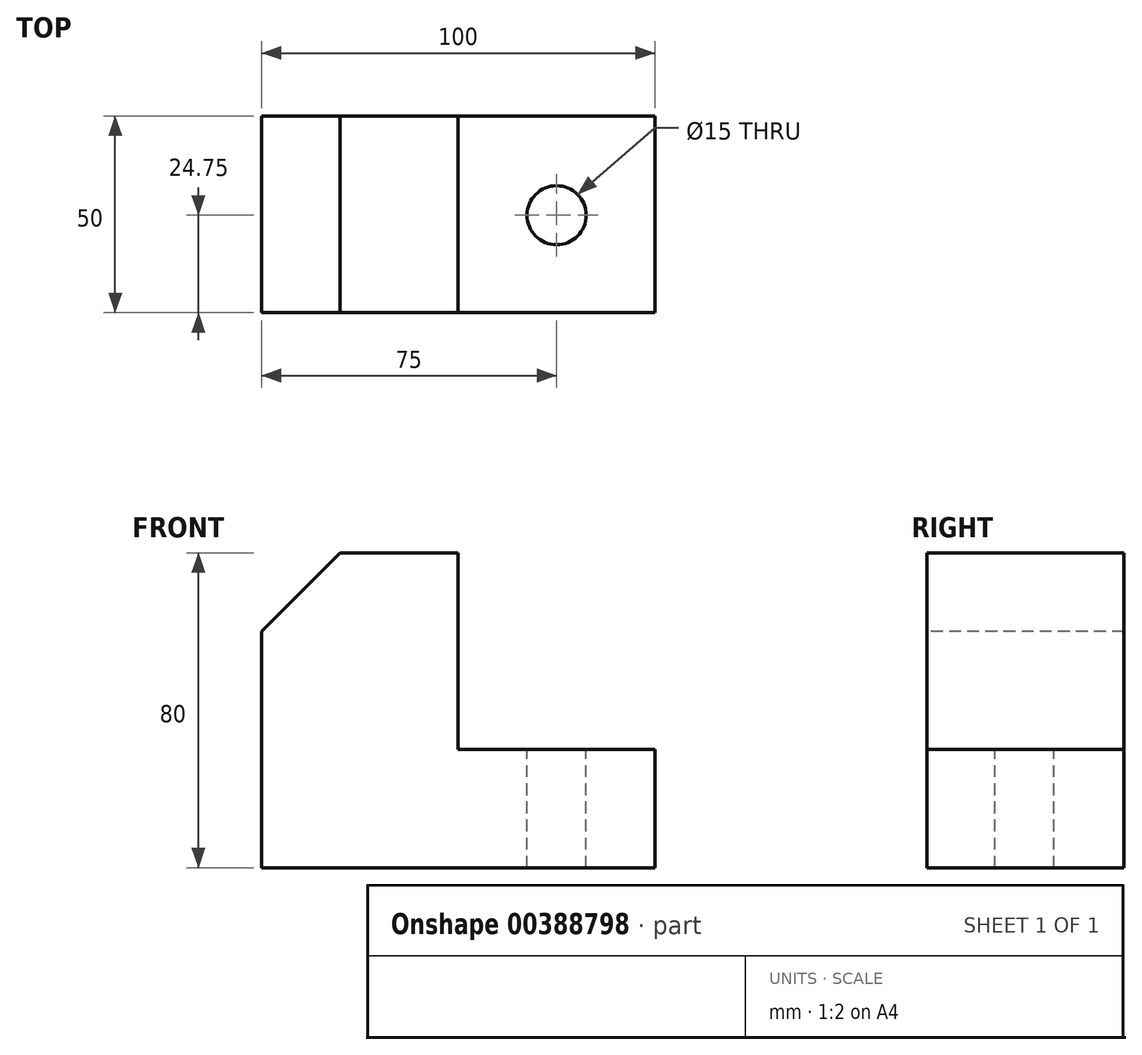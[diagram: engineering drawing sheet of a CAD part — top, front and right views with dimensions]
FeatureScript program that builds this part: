
annotation { "Feature Type Name" : "Feature", "Feature Type Description" : "" }
export const myFeature = defineFeature(function(context is Context, id is Id, definition is map)
    precondition{}
    {
        {
            var Q0;
            Q0=qCreatedBy(makeId("Top.planeOp"),FACE);
            var sketch = newSketch(context, id + "F0", { "sketchPlane" : qUnion([Q0])});
            skLineSegment(sketch, "E0.bottom", {"start": v(0, 0) * mm, "end": v(100, 0) * mm});
            skLineSegment(sketch, "E0.top", {"start": v(0, 50) * mm, "end": v(100, 50) * mm});
            skLineSegment(sketch, "E0.left", {"start": v(0, 0) * mm, "end": v(0, 50) * mm});
            skLineSegment(sketch, "E0.right", {"start": v(100, 0) * mm, "end": v(100, 50) * mm});
            skSolve(sketch);
        }
        {
            var Q0;
            Q0=makeQuery(id+"F0.imprint","IMPRINT",FACE,{"disambiguationData":[TD([[makeQuery(id+"F0.imprint","IMPRINT",EDGE,{"derivedFrom":sQuery(id+"F0.wireOp",EDGE,"E0.bottom")}),1.0]])]});
            extrude(context, id + "F1", {"entities" : qUnion([Q0]), "depth" : 30 * mm});
        }
        {
            var Q0;
            Q0=makeQuery(id+"F1.opExtrude","CAP_FACE",FACE,{"disambiguationData":[OSD([sQuery(id+"F0.wireOp",EDGE,"E0.bottom"),sQuery(id+"F0.wireOp",EDGE,"E0.top"),sQuery(id+"F0.wireOp",EDGE,"E0.left"),sQuery(id+"F0.wireOp",EDGE,"E0.right")])],"isStart":false});
            var sketch = newSketch(context, id + "F2", { "sketchPlane" : qUnion([Q0])});
            skLineSegment(sketch, "E1.bottom", {"start": v(0, 0) * mm, "end": v(50, 0) * mm});
            skLineSegment(sketch, "E1.top", {"start": v(0, 50) * mm, "end": v(50, 50) * mm});
            skLineSegment(sketch, "E1.left", {"start": v(0, 0) * mm, "end": v(0, 50) * mm});
            skLineSegment(sketch, "E1.right", {"start": v(50, 0) * mm, "end": v(50, 50) * mm});
            skSolve(sketch);
        }
        {
            var Q0;
            Q0 = qSketchRegion(id + "F2", true);
            extrude(context, id + "F3", {"entities" : qUnion([Q0]), "operationType" : NewBodyOperationType.ADD, "depth" : 50 * mm});
        }
        {
            var Q0;
            Q0=makeQuery(id+"F3.boolean.opBoolean","MERGE",FACE,{"derivedFrom":[makeQuery(id+"F1.opExtrude","SWEPT_FACE",FACE,{"disambiguationData":[OSD([sQuery(id+"F0.wireOp",EDGE,"E0.bottom")])]}),makeQuery(id+"F3.opExtrude","SWEPT_FACE",FACE,{"disambiguationData":[OSD([sQuery(id+"F2.wireOp",EDGE,"E1.bottom")])]})]});
            var sketch = newSketch(context, id + "F4", { "sketchPlane" : qUnion([Q0])});
            skLineSegment(sketch, "E2", {"start": v(0, 80) * mm, "end": v(20, 80) * mm});
            skLineSegment(sketch, "E3", {"start": v(20, 80) * mm, "end": v(0, 60) * mm});
            skSolve(sketch);
        }
        {
            var Q0;
            Q0 = qSketchRegion(id + "F4", true);
            var Q1;
            {var subQ0=sQuery(id+"F4.wireOp",EDGE,"E2");Q1=makeQuery(id+"F4.imprint","IMPRINT",FACE,{"disambiguationData":[TD([[makeQuery(id+"F4.imprint","IMPRINT",EDGE,{"derivedFrom":subQ0}),-1.0]])]});}
            extrude(context, id + "F5", {"entities" : qUnion([Q0, Q1]), "operationType" : NewBodyOperationType.REMOVE, "endBound" : BoundingType.UP_TO_NEXT, "oppositeDirection" : true, "depth" : 25 * mm});
        }
        {
            var Q0;
            Q0=makeQuery(id+"F1.opExtrude","CAP_FACE",FACE,{"disambiguationData":[OSD([sQuery(id+"F0.wireOp",EDGE,"E0.bottom"),sQuery(id+"F0.wireOp",EDGE,"E0.top"),sQuery(id+"F0.wireOp",EDGE,"E0.left"),sQuery(id+"F0.wireOp",EDGE,"E0.right")])],"isStart":false});
            var sketch = newSketch(context, id + "F6", { "sketchPlane" : qUnion([Q0])});
            skCircle(sketch, "E4", {"center": v(75, 24.75) * mm, "radius": 7.5 * mm});
            skSolve(sketch);
        }
        {
            var Q0;
            Q0 = qSketchRegion(id + "F6", true);
            extrude(context, id + "F7", {"entities" : qUnion([Q0]), "operationType" : NewBodyOperationType.REMOVE, "endBound" : BoundingType.UP_TO_NEXT, "oppositeDirection" : true, "depth" : 25 * mm});
        }
    });
